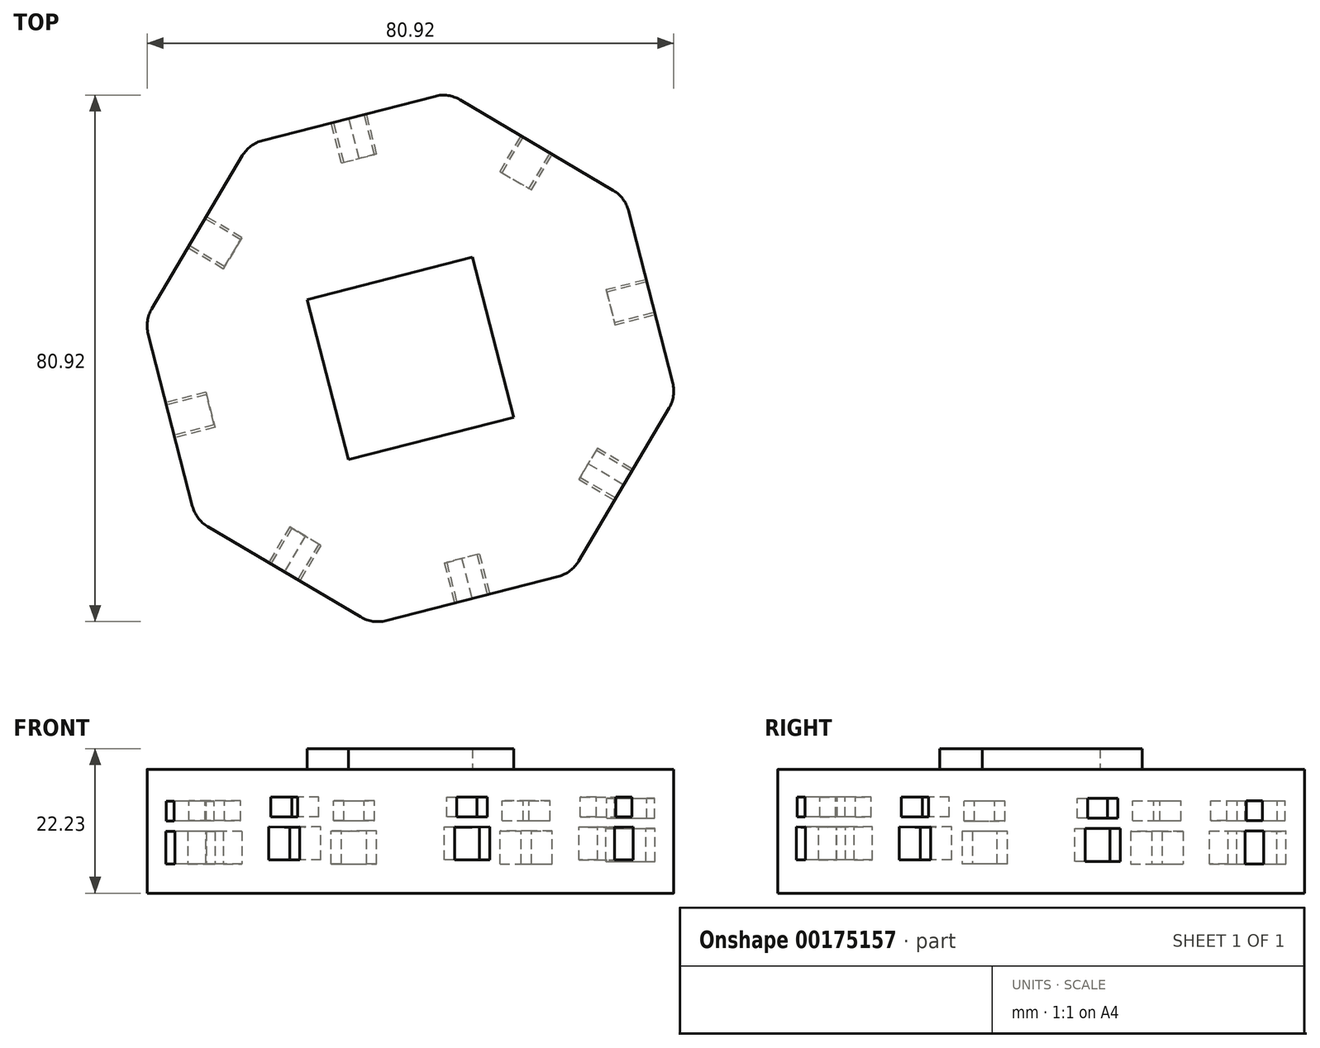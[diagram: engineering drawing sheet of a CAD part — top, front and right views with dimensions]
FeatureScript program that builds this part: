
annotation { "Feature Type Name" : "Feature", "Feature Type Description" : "" }
export const myFeature = defineFeature(function(context is Context, id is Id, definition is map)
    precondition{}
    {
        {
            var Q0;
            Q0=qCreatedBy(makeId("Top.planeOp"),FACE);
            var sketch = newSketch(context, id + "F0", { "sketchPlane" : qUnion([Q0])});
            skCircle(sketch, "E0.cCircle", {"center": v(0, 0) * mm, "radius": 38.1 * mm, "construction": true});
            skLineSegment(sketch, "E0.0", {"start": v(-40.83, 5.82) * mm, "end": v(-24.75, 32.98) * mm});
            skLineSegment(sketch, "E0.1", {"start": v(-24.75, 32.98) * mm, "end": v(5.82, 40.83) * mm});
            skLineSegment(sketch, "E0.2", {"start": v(5.82, 40.83) * mm, "end": v(32.98, 24.75) * mm});
            skLineSegment(sketch, "E0.3", {"start": v(32.98, 24.75) * mm, "end": v(40.83, -5.82) * mm});
            skLineSegment(sketch, "E0.4", {"start": v(40.83, -5.82) * mm, "end": v(24.75, -32.98) * mm});
            skLineSegment(sketch, "E0.5", {"start": v(24.75, -32.98) * mm, "end": v(-5.82, -40.83) * mm});
            skLineSegment(sketch, "E0.6", {"start": v(-5.82, -40.83) * mm, "end": v(-32.98, -24.75) * mm});
            skLineSegment(sketch, "E0.7", {"start": v(-32.98, -24.75) * mm, "end": v(-40.83, 5.82) * mm});
            skPoint(sketch, "E0.0.midPoint", {"position": v(-32.8, 19.4) * mm});
            skLineSegment(sketch, "E1", {"start": v(32.8, -19.4) * mm, "end": v(-32.8, 19.4) * mm});
            skLineSegment(sketch, "E2", {"start": v(9.47, -36.9) * mm, "end": v(-9.47, 36.9) * mm});
            skLineSegment(sketch, "E3", {"start": v(19.4, 32.8) * mm, "end": v(-19.4, -32.8) * mm});
            skLineSegment(sketch, "E4", {"start": v(36.9, 9.47) * mm, "end": v(-36.9, -9.47) * mm});
            skSolve(sketch);
        }
        {
            var Q0;
            Q0=makeQuery(id+"F0.imprint","IMPRINT",FACE,{"disambiguationData":[TD([[makeQuery(id+"F0.imprint","IMPRINT",EDGE,{"derivedFrom":sQuery(id+"F0.wireOp",EDGE,"E0.0")}),-1.0]])]});
            var Q1;
            {var subQ0=sQuery(id+"F0.wireOp",EDGE,"E0.2");var subQ1=sQuery(id+"F0.wireOp",EDGE,"E0.1");var subQ2=makeQuery(id+"F0.imprint","INTERSECT",VERTEX,{"derivedFrom":[subQ1,subQ0]});Q1=makeQuery(id+"F0.imprint","IMPRINT",FACE,{"disambiguationData":[TD([[makeQuery(id+"F0.imprint","IMPRINT",EDGE,{"disambiguationData":[TD([[subQ2,1.0]])],"derivedFrom":subQ1}),-1.0]])]});}
            var Q2;
            {var subQ0=sQuery(id+"F0.wireOp",EDGE,"E0.3");var subQ1=sQuery(id+"F0.wireOp",EDGE,"E0.2");var subQ2=makeQuery(id+"F0.imprint","INTERSECT",VERTEX,{"derivedFrom":[subQ1,subQ0]});Q2=makeQuery(id+"F0.imprint","IMPRINT",FACE,{"disambiguationData":[TD([[makeQuery(id+"F0.imprint","IMPRINT",EDGE,{"disambiguationData":[TD([[subQ2,1.0]])],"derivedFrom":subQ1}),-1.0]])]});}
            var Q3;
            {var subQ0=sQuery(id+"F0.wireOp",EDGE,"E0.4");var subQ1=sQuery(id+"F0.wireOp",EDGE,"E0.3");var subQ2=makeQuery(id+"F0.imprint","INTERSECT",VERTEX,{"derivedFrom":[subQ1,subQ0]});Q3=makeQuery(id+"F0.imprint","IMPRINT",FACE,{"disambiguationData":[TD([[makeQuery(id+"F0.imprint","IMPRINT",EDGE,{"disambiguationData":[TD([[subQ2,1.0]])],"derivedFrom":subQ1}),-1.0]])]});}
            var Q4;
            {var subQ0=sQuery(id+"F0.wireOp",EDGE,"E0.5");var subQ1=sQuery(id+"F0.wireOp",EDGE,"E0.4");var subQ2=makeQuery(id+"F0.imprint","INTERSECT",VERTEX,{"derivedFrom":[subQ1,subQ0]});Q4=makeQuery(id+"F0.imprint","IMPRINT",FACE,{"disambiguationData":[TD([[makeQuery(id+"F0.imprint","IMPRINT",EDGE,{"disambiguationData":[TD([[subQ2,1.0]])],"derivedFrom":subQ1}),-1.0]])]});}
            var Q5;
            {var subQ0=sQuery(id+"F0.wireOp",EDGE,"E0.6");var subQ1=sQuery(id+"F0.wireOp",EDGE,"E0.5");var subQ2=makeQuery(id+"F0.imprint","INTERSECT",VERTEX,{"derivedFrom":[subQ1,subQ0]});Q5=makeQuery(id+"F0.imprint","IMPRINT",FACE,{"disambiguationData":[TD([[makeQuery(id+"F0.imprint","IMPRINT",EDGE,{"disambiguationData":[TD([[subQ2,1.0]])],"derivedFrom":subQ1}),-1.0]])]});}
            var Q6;
            {var subQ0=sQuery(id+"F0.wireOp",EDGE,"E0.7");var subQ1=sQuery(id+"F0.wireOp",EDGE,"E0.6");var subQ2=makeQuery(id+"F0.imprint","INTERSECT",VERTEX,{"derivedFrom":[subQ1,subQ0]});Q6=makeQuery(id+"F0.imprint","IMPRINT",FACE,{"disambiguationData":[TD([[makeQuery(id+"F0.imprint","IMPRINT",EDGE,{"disambiguationData":[TD([[subQ2,1.0]])],"derivedFrom":subQ1}),-1.0]])]});}
            extrude(context, id + "F1", {"entities" : qUnion([Q0, Q1, Q2, Q3, Q4, Q5, Q6]), "endBound" : BoundingType.SYMMETRIC, "depth" : 19.05 * mm});
        }
        {
            var Q0;
            Q0=makeQuery(id+"F1.opExtrude","SWEPT_FACE",FACE,{"disambiguationData":[OSD([sQuery(id+"F0.wireOp",EDGE,"E0.7")])]});
            var sketch = newSketch(context, id + "F2", { "sketchPlane" : qUnion([Q0])});
            skPoint(sketch, "E5.middle", {"position": v(0, 0) * mm});
            skPoint(sketch, "E6", {"position": v(0, -5.06) * mm});
            skLineSegment(sketch, "E7", {"start": v(-2.8, -2.52) * mm, "end": v(-2.8, 0) * mm});
            skLineSegment(sketch, "E8", {"start": v(2.8, -2.52) * mm, "end": v(2.8, 0) * mm});
            skLineSegment(sketch, "E9", {"start": v(-2.8, 0) * mm, "end": v(2.8, 0) * mm});
            skLineSegment(sketch, "E10.MirrorCS", {"start": v(-2.8, -2.52) * mm, "end": v(-2.8, -5.04) * mm});
            skLineSegment(sketch, "E11.MirrorCS", {"start": v(-2.8, -5.04) * mm, "end": v(2.8, -5.04) * mm});
            skLineSegment(sketch, "E12.MirrorCS", {"start": v(2.8, -2.52) * mm, "end": v(2.8, -5.04) * mm});
            skPoint(sketch, "E13", {"position": v(0, 1.56) * mm});
            skLineSegment(sketch, "E14", {"start": v(0, 1.56) * mm, "end": v(-2.41, 1.56) * mm});
            skLineSegment(sketch, "E15.MirrorCS", {"start": v(0, 1.56) * mm, "end": v(2.41, 1.56) * mm});
            skLineSegment(sketch, "E16", {"start": v(2.41, 1.56) * mm, "end": v(2.41, 4.6) * mm});
            skLineSegment(sketch, "E17.MirrorCS", {"start": v(-2.41, 1.56) * mm, "end": v(-2.41, 4.6) * mm});
            skLineSegment(sketch, "E18", {"start": v(-2.41, 4.6) * mm, "end": v(2.41, 4.6) * mm});
            skSolve(sketch);
        }
        {
            var Q0;
            Q0 = qSketchRegion(id + "F2", true);
            extrude(context, id + "F3", {"entities" : qUnion([Q0]), "operationType" : NewBodyOperationType.REMOVE, "oppositeDirection" : true, "depth" : 6.35 * mm});
        }
        {
            var Q0;
            Q0=makeQuery(id+"F1.opExtrude","SWEPT_FACE",FACE,{"disambiguationData":[OSD([sQuery(id+"F0.wireOp",EDGE,"E0.1")])]});
            var sketch = newSketch(context, id + "F4", { "sketchPlane" : qUnion([Q0])});
            skPoint(sketch, "E19", {"position": v(0, -9.53) * mm});
            skPoint(sketch, "E20", {"position": v(0, -5.04) * mm});
            skPoint(sketch, "E21", {"position": v(0, 1.6) * mm});
            skLineSegment(sketch, "E22", {"start": v(0, 1.6) * mm, "end": v(2.41, 1.6) * mm});
            skLineSegment(sketch, "E23", {"start": v(2.41, 1.6) * mm, "end": v(2.41, 4.64) * mm});
            skLineSegment(sketch, "E24", {"start": v(2.41, 4.64) * mm, "end": v(0, 4.64) * mm});
            skLineSegment(sketch, "E25.MirrorCS", {"start": v(-2.41, 4.64) * mm, "end": v(0, 4.64) * mm});
            skLineSegment(sketch, "E26.MirrorCS", {"start": v(-2.41, 1.6) * mm, "end": v(-2.41, 4.64) * mm});
            skLineSegment(sketch, "E27.MirrorCS", {"start": v(0, 1.6) * mm, "end": v(-2.41, 1.6) * mm});
            skLineSegment(sketch, "E28", {"start": v(0, -5.04) * mm, "end": v(2.8, -5.04) * mm});
            skLineSegment(sketch, "E29", {"start": v(2.8, -5.04) * mm, "end": v(2.8, 0.04) * mm});
            skLineSegment(sketch, "E30", {"start": v(2.8, 0.04) * mm, "end": v(0, 0) * mm});
            skLineSegment(sketch, "E31.MirrorCS", {"start": v(-2.8, 0.04) * mm, "end": v(0, 0) * mm});
            skLineSegment(sketch, "E32.MirrorCS", {"start": v(-2.8, -5.04) * mm, "end": v(-2.8, 0.04) * mm});
            skLineSegment(sketch, "E33.MirrorCS", {"start": v(0, -5.04) * mm, "end": v(-2.8, -5.04) * mm});
            skSolve(sketch);
        }
        {
            var Q0;
            Q0=makeQuery(id+"F4.imprint","IMPRINT",FACE,{"disambiguationData":[TD([[makeQuery(id+"F4.imprint","IMPRINT",EDGE,{"derivedFrom":sQuery(id+"F4.wireOp",EDGE,"LZL7hc5V-V0Lx-cx1U-TuNf-BSn2dO84Y1Hg")}),-1.0]])]});
            var Q1;
            Q1=makeQuery(id+"F4.imprint","IMPRINT",FACE,{"disambiguationData":[TD([[makeQuery(id+"F4.imprint","IMPRINT",EDGE,{"derivedFrom":sQuery(id+"F4.wireOp",EDGE,"E28")}),1.0]])]});
            var Q2;
            Q2=makeQuery(id+"F4.imprint","IMPRINT",FACE,{"disambiguationData":[TD([[makeQuery(id+"F4.imprint","IMPRINT",EDGE,{"derivedFrom":sQuery(id+"F4.wireOp",EDGE,"E22")}),1.0]])]});
            extrude(context, id + "F5", {"entities" : qUnion([Q0, Q1, Q2]), "operationType" : NewBodyOperationType.REMOVE, "oppositeDirection" : true, "depth" : 6.35 * mm});
        }
        {
            var Q0;
            Q0=makeQuery(id+"F1.opExtrude","SWEPT_FACE",FACE,{"disambiguationData":[OSD([sQuery(id+"F0.wireOp",EDGE,"E0.0")])]});
            var sketch = newSketch(context, id + "F6", { "sketchPlane" : qUnion([Q0])});
            skPoint(sketch, "E34", {"position": v(0, -5.04) * mm});
            skLineSegment(sketch, "E35", {"start": v(0, -5.04) * mm, "end": v(2.8, -5.04) * mm});
            skLineSegment(sketch, "E36", {"start": v(2.8, 0) * mm, "end": v(2.8, -5.04) * mm});
            skLineSegment(sketch, "E37.MirrorCS", {"start": v(-2.8, 0) * mm, "end": v(-2.8, -5.04) * mm});
            skLineSegment(sketch, "E38.MirrorCS", {"start": v(0, -5.04) * mm, "end": v(-2.8, -5.04) * mm});
            skPoint(sketch, "E39", {"position": v(0, 1.6) * mm});
            skLineSegment(sketch, "E40", {"start": v(-2.8, 0) * mm, "end": v(2.8, 0) * mm});
            skLineSegment(sketch, "E41", {"start": v(0, 1.6) * mm, "end": v(2.41, 1.6) * mm});
            skLineSegment(sketch, "E42", {"start": v(2.41, 1.6) * mm, "end": v(2.41, 4.64) * mm});
            skLineSegment(sketch, "E43", {"start": v(2.41, 4.64) * mm, "end": v(0, 4.64) * mm});
            skLineSegment(sketch, "E44.MirrorCS", {"start": v(-2.41, 4.64) * mm, "end": v(0, 4.64) * mm});
            skLineSegment(sketch, "E45.MirrorCS", {"start": v(-2.41, 1.6) * mm, "end": v(-2.41, 4.64) * mm});
            skLineSegment(sketch, "E46.MirrorCS", {"start": v(0, 1.6) * mm, "end": v(-2.41, 1.6) * mm});
            skSolve(sketch);
        }
        {
            var Q0;
            Q0=makeQuery(id+"F6.imprint","IMPRINT",FACE,{"disambiguationData":[TD([[makeQuery(id+"F6.imprint","IMPRINT",EDGE,{"derivedFrom":sQuery(id+"F6.wireOp",EDGE,"E41")}),1.0]])]});
            var Q1;
            Q1=makeQuery(id+"F6.imprint","IMPRINT",FACE,{"disambiguationData":[TD([[makeQuery(id+"F6.imprint","IMPRINT",EDGE,{"derivedFrom":sQuery(id+"F6.wireOp",EDGE,"E35")}),1.0]])]});
            extrude(context, id + "F7", {"entities" : qUnion([Q0, Q1]), "operationType" : NewBodyOperationType.REMOVE, "oppositeDirection" : true, "depth" : 6.35 * mm});
        }
        {
            var Q0;
            Q0=makeQuery(id+"F1.opExtrude","SWEPT_FACE",FACE,{"disambiguationData":[OSD([sQuery(id+"F0.wireOp",EDGE,"E0.2")])]});
            var sketch = newSketch(context, id + "F8", { "sketchPlane" : qUnion([Q0])});
            skPoint(sketch, "E47", {"position": v(0, -5.04) * mm});
            skLineSegment(sketch, "E48", {"start": v(0, -5.04) * mm, "end": v(2.8, -5.04) * mm});
            skLineSegment(sketch, "E49", {"start": v(2.8, -5.04) * mm, "end": v(2.8, 0.04) * mm});
            skLineSegment(sketch, "E50.MirrorCS", {"start": v(-2.8, -5.04) * mm, "end": v(-2.8, 0.04) * mm});
            skLineSegment(sketch, "E51.MirrorCS", {"start": v(0, -5.04) * mm, "end": v(-2.8, -5.04) * mm});
            skLineSegment(sketch, "E52", {"start": v(-2.8, 0.04) * mm, "end": v(2.8, 0.04) * mm});
            skPoint(sketch, "E53", {"position": v(0, 1.63) * mm});
            skLineSegment(sketch, "E54", {"start": v(0, 1.63) * mm, "end": v(2.41, 1.63) * mm});
            skLineSegment(sketch, "E55", {"start": v(2.41, 1.63) * mm, "end": v(2.41, 4.68) * mm});
            skLineSegment(sketch, "E56.MirrorCS", {"start": v(0, 1.63) * mm, "end": v(-2.41, 1.63) * mm});
            skLineSegment(sketch, "E57.MirrorCS", {"start": v(-2.41, 1.63) * mm, "end": v(-2.41, 4.68) * mm});
            skLineSegment(sketch, "E58", {"start": v(-2.41, 4.68) * mm, "end": v(2.41, 4.68) * mm});
            skSolve(sketch);
        }
        {
            var Q0;
            Q0=makeQuery(id+"F8.imprint","IMPRINT",FACE,{"disambiguationData":[TD([[makeQuery(id+"F8.imprint","IMPRINT",EDGE,{"derivedFrom":sQuery(id+"F8.wireOp",EDGE,"E54")}),1.0]])]});
            var Q1;
            Q1=makeQuery(id+"F8.imprint","IMPRINT",FACE,{"disambiguationData":[TD([[makeQuery(id+"F8.imprint","IMPRINT",EDGE,{"derivedFrom":sQuery(id+"F8.wireOp",EDGE,"E48")}),1.0]])]});
            extrude(context, id + "F9", {"entities" : qUnion([Q0, Q1]), "operationType" : NewBodyOperationType.REMOVE, "oppositeDirection" : true, "depth" : 6.35 * mm});
        }
        {
            var Q0;
            Q0=makeQuery(id+"F1.opExtrude","SWEPT_FACE",FACE,{"disambiguationData":[OSD([sQuery(id+"F0.wireOp",EDGE,"E0.3")])]});
            var sketch = newSketch(context, id + "F10", { "sketchPlane" : qUnion([Q0])});
            skPoint(sketch, "E59", {"position": v(0, -4.7) * mm});
            skLineSegment(sketch, "E60", {"start": v(0, -4.7) * mm, "end": v(2.8, -4.7) * mm});
            skLineSegment(sketch, "E61", {"start": v(2.8, -4.7) * mm, "end": v(2.8, 0.39) * mm});
            skLineSegment(sketch, "E62.MirrorCS", {"start": v(-2.8, -4.7) * mm, "end": v(-2.8, 0.39) * mm});
            skLineSegment(sketch, "E63.MirrorCS", {"start": v(0, -4.7) * mm, "end": v(-2.8, -4.7) * mm});
            skLineSegment(sketch, "E64", {"start": v(-2.8, 0.39) * mm, "end": v(2.8, 0.39) * mm});
            skPoint(sketch, "E65", {"position": v(0, 1.98) * mm});
            skLineSegment(sketch, "E66", {"start": v(0, 1.98) * mm, "end": v(2.41, 1.98) * mm});
            skLineSegment(sketch, "E67", {"start": v(2.41, 1.98) * mm, "end": v(2.41, 5.03) * mm});
            skLineSegment(sketch, "E68.MirrorCS", {"start": v(0, 1.98) * mm, "end": v(-2.41, 1.98) * mm});
            skLineSegment(sketch, "E69.MirrorCS", {"start": v(-2.41, 1.98) * mm, "end": v(-2.41, 5.03) * mm});
            skLineSegment(sketch, "E70", {"start": v(-2.41, 5.03) * mm, "end": v(2.41, 5.03) * mm});
            skSolve(sketch);
        }
        {
            var Q0;
            Q0 = qSketchRegion(id + "F10", true);
            extrude(context, id + "F11", {"entities" : qUnion([Q0]), "operationType" : NewBodyOperationType.REMOVE, "oppositeDirection" : true, "depth" : 6.35 * mm});
        }
        {
            var Q0;
            Q0=makeQuery(id+"F1.opExtrude","SWEPT_FACE",FACE,{"disambiguationData":[OSD([sQuery(id+"F0.wireOp",EDGE,"E0.4")])]});
            var sketch = newSketch(context, id + "F12", { "sketchPlane" : qUnion([Q0])});
            skPoint(sketch, "E71", {"position": v(0, -8.9) * mm});
            skPoint(sketch, "E72", {"position": v(0, -4.42) * mm});
            skPoint(sketch, "E73", {"position": v(0, 2.22) * mm});
            skLineSegment(sketch, "E74", {"start": v(0, 2.22) * mm, "end": v(2.41, 2.22) * mm});
            skLineSegment(sketch, "E75", {"start": v(2.41, 2.22) * mm, "end": v(2.41, 5.26) * mm});
            skLineSegment(sketch, "E76", {"start": v(2.41, 5.26) * mm, "end": v(0, 5.26) * mm});
            skLineSegment(sketch, "E77.MirrorCS", {"start": v(-2.41, 5.26) * mm, "end": v(0, 5.26) * mm});
            skLineSegment(sketch, "E78.MirrorCS", {"start": v(-2.41, 2.22) * mm, "end": v(-2.41, 5.26) * mm});
            skLineSegment(sketch, "E79.MirrorCS", {"start": v(0, 2.22) * mm, "end": v(-2.41, 2.22) * mm});
            skLineSegment(sketch, "E80", {"start": v(0, -4.42) * mm, "end": v(2.8, -4.42) * mm});
            skLineSegment(sketch, "E81", {"start": v(2.8, -4.42) * mm, "end": v(2.8, 0.66) * mm});
            skLineSegment(sketch, "E82", {"start": v(2.8, 0.66) * mm, "end": v(0, 0.62) * mm});
            skLineSegment(sketch, "E83.MirrorCS", {"start": v(-2.8, 0.66) * mm, "end": v(0, 0.62) * mm});
            skLineSegment(sketch, "E84.MirrorCS", {"start": v(-2.8, -4.42) * mm, "end": v(-2.8, 0.66) * mm});
            skLineSegment(sketch, "E85.MirrorCS", {"start": v(0, -4.42) * mm, "end": v(-2.8, -4.42) * mm});
            skSolve(sketch);
        }
        {
            var Q0;
            Q0=makeQuery(id+"F12.imprint","IMPRINT",FACE,{"disambiguationData":[TD([[makeQuery(id+"F12.imprint","IMPRINT",EDGE,{"derivedFrom":sQuery(id+"F12.wireOp",EDGE,"E80")}),1.0]])]});
            var Q1;
            Q1=makeQuery(id+"F12.imprint","IMPRINT",FACE,{"disambiguationData":[TD([[makeQuery(id+"F12.imprint","IMPRINT",EDGE,{"derivedFrom":sQuery(id+"F12.wireOp",EDGE,"E74")}),1.0]])]});
            extrude(context, id + "F13", {"entities" : qUnion([Q0, Q1]), "operationType" : NewBodyOperationType.REMOVE, "oppositeDirection" : true, "depth" : 6.35 * mm});
        }
        {
            var Q0;
            Q0=makeQuery(id+"F1.opExtrude","SWEPT_FACE",FACE,{"disambiguationData":[OSD([sQuery(id+"F0.wireOp",EDGE,"E0.5")])]});
            var sketch = newSketch(context, id + "F14", { "sketchPlane" : qUnion([Q0])});
            skPoint(sketch, "E86", {"position": v(0, -8.9) * mm});
            skPoint(sketch, "E87", {"position": v(0, -4.42) * mm});
            skPoint(sketch, "E88", {"position": v(0, 2.22) * mm});
            skLineSegment(sketch, "E89", {"start": v(0, 2.22) * mm, "end": v(2.41, 2.22) * mm});
            skLineSegment(sketch, "E90", {"start": v(2.41, 2.22) * mm, "end": v(2.41, 5.26) * mm});
            skLineSegment(sketch, "E91", {"start": v(2.41, 5.26) * mm, "end": v(0, 5.26) * mm});
            skLineSegment(sketch, "E92.MirrorCS", {"start": v(-2.41, 5.26) * mm, "end": v(0, 5.26) * mm});
            skLineSegment(sketch, "E93.MirrorCS", {"start": v(-2.41, 2.22) * mm, "end": v(-2.41, 5.26) * mm});
            skLineSegment(sketch, "E94.MirrorCS", {"start": v(0, 2.22) * mm, "end": v(-2.41, 2.22) * mm});
            skLineSegment(sketch, "E95", {"start": v(0, -4.42) * mm, "end": v(2.8, -4.42) * mm});
            skLineSegment(sketch, "E96", {"start": v(2.8, -4.42) * mm, "end": v(2.8, 0.66) * mm});
            skLineSegment(sketch, "E97", {"start": v(2.8, 0.66) * mm, "end": v(0, 0.62) * mm});
            skLineSegment(sketch, "E98.MirrorCS", {"start": v(-2.8, 0.66) * mm, "end": v(0, 0.62) * mm});
            skLineSegment(sketch, "E99.MirrorCS", {"start": v(-2.8, -4.42) * mm, "end": v(-2.8, 0.66) * mm});
            skLineSegment(sketch, "E100.MirrorCS", {"start": v(0, -4.42) * mm, "end": v(-2.8, -4.42) * mm});
            skSolve(sketch);
        }
        {
            var Q0;
            Q0=makeQuery(id+"F14.imprint","IMPRINT",FACE,{"disambiguationData":[TD([[makeQuery(id+"F14.imprint","IMPRINT",EDGE,{"derivedFrom":sQuery(id+"F14.wireOp",EDGE,"E95")}),1.0]])]});
            var Q1;
            Q1=makeQuery(id+"F14.imprint","IMPRINT",FACE,{"disambiguationData":[TD([[makeQuery(id+"F14.imprint","IMPRINT",EDGE,{"derivedFrom":sQuery(id+"F14.wireOp",EDGE,"E89")}),1.0]])]});
            extrude(context, id + "F15", {"entities" : qUnion([Q0, Q1]), "operationType" : NewBodyOperationType.REMOVE, "oppositeDirection" : true, "depth" : 6.35 * mm});
        }
        {
            var Q0;
            Q0=makeQuery(id+"F1.opExtrude","SWEPT_FACE",FACE,{"disambiguationData":[OSD([sQuery(id+"F0.wireOp",EDGE,"E0.6")])]});
            var sketch = newSketch(context, id + "F16", { "sketchPlane" : qUnion([Q0])});
            skPoint(sketch, "E101", {"position": v(0, -8.9) * mm});
            skPoint(sketch, "E102", {"position": v(0, -4.42) * mm});
            skPoint(sketch, "E103", {"position": v(0, 2.22) * mm});
            skLineSegment(sketch, "E104", {"start": v(0, 2.22) * mm, "end": v(2.41, 2.22) * mm});
            skLineSegment(sketch, "E105", {"start": v(2.41, 2.22) * mm, "end": v(2.41, 5.26) * mm});
            skLineSegment(sketch, "E106", {"start": v(2.41, 5.26) * mm, "end": v(0, 5.26) * mm});
            skLineSegment(sketch, "E107.MirrorCS", {"start": v(-2.41, 5.26) * mm, "end": v(0, 5.26) * mm});
            skLineSegment(sketch, "E108.MirrorCS", {"start": v(-2.41, 2.22) * mm, "end": v(-2.41, 5.26) * mm});
            skLineSegment(sketch, "E109.MirrorCS", {"start": v(0, 2.22) * mm, "end": v(-2.41, 2.22) * mm});
            skLineSegment(sketch, "E110", {"start": v(0, -4.42) * mm, "end": v(2.8, -4.42) * mm});
            skLineSegment(sketch, "E111", {"start": v(2.8, -4.42) * mm, "end": v(2.8, 0.66) * mm});
            skLineSegment(sketch, "E112", {"start": v(2.8, 0.66) * mm, "end": v(0, 0.62) * mm});
            skLineSegment(sketch, "E113.MirrorCS", {"start": v(-2.8, 0.66) * mm, "end": v(0, 0.62) * mm});
            skLineSegment(sketch, "E114.MirrorCS", {"start": v(-2.8, -4.42) * mm, "end": v(-2.8, 0.66) * mm});
            skLineSegment(sketch, "E115.MirrorCS", {"start": v(0, -4.42) * mm, "end": v(-2.8, -4.42) * mm});
            skSolve(sketch);
        }
        {
            var Q0;
            Q0=makeQuery(id+"F16.imprint","IMPRINT",FACE,{"disambiguationData":[TD([[makeQuery(id+"F16.imprint","IMPRINT",EDGE,{"derivedFrom":sQuery(id+"F16.wireOp",EDGE,"E104")}),1.0]])]});
            var Q1;
            Q1=makeQuery(id+"F16.imprint","IMPRINT",FACE,{"disambiguationData":[TD([[makeQuery(id+"F16.imprint","IMPRINT",EDGE,{"derivedFrom":sQuery(id+"F16.wireOp",EDGE,"E110")}),1.0]])]});
            extrude(context, id + "F17", {"entities" : qUnion([Q0, Q1]), "operationType" : NewBodyOperationType.REMOVE, "oppositeDirection" : true, "depth" : 6.35 * mm});
        }
        {
            var Q0;
            Q0=makeQuery(id+"F1.opExtrude","CAP_FACE",FACE,{"disambiguationData":[OSD([sQuery(id+"F0.wireOp",EDGE,"E0.0"),sQuery(id+"F0.wireOp",EDGE,"E0.1"),sQuery(id+"F0.wireOp",EDGE,"E0.2"),sQuery(id+"F0.wireOp",EDGE,"E0.3"),sQuery(id+"F0.wireOp",EDGE,"E0.4"),sQuery(id+"F0.wireOp",EDGE,"E0.5"),sQuery(id+"F0.wireOp",EDGE,"E0.6"),sQuery(id+"F0.wireOp",EDGE,"E0.7")])],"isStart":false});
            var sketch = newSketch(context, id + "F18", { "sketchPlane" : qUnion([Q0])});
            skLineSegment(sketch, "E116", {"start": v(-24.75, 32.98) * mm, "end": v(-5.82, -40.83) * mm});
            skLineSegment(sketch, "E117", {"start": v(5.82, 40.83) * mm, "end": v(24.75, -32.98) * mm});
            skLineSegment(sketch, "E118", {"start": v(3.16, -12.3) * mm, "end": v(-12.13, -16.22) * mm});
            skLineSegment(sketch, "E119", {"start": v(3.16, -12.3) * mm, "end": v(18.44, -8.38) * mm});
            skLineSegment(sketch, "E120", {"start": v(-3.16, 12.3) * mm, "end": v(-18.44, 8.38) * mm});
            skLineSegment(sketch, "E121", {"start": v(-3.16, 12.3) * mm, "end": v(12.13, 16.22) * mm});
            skPoint(sketch, "E122", {"position": v(-15.86, 9.04) * mm});
            skPoint(sketch, "E123", {"position": v(9.54, 15.56) * mm});
            skPoint(sketch, "E124", {"position": v(-9.54, -15.56) * mm});
            skPoint(sketch, "E125", {"position": v(15.86, -9.04) * mm});
            skLineSegment(sketch, "E126", {"start": v(-15.86, 9.04) * mm, "end": v(-9.54, -15.56) * mm});
            skLineSegment(sketch, "E127", {"start": v(9.54, 15.56) * mm, "end": v(15.86, -9.04) * mm});
            skSolve(sketch);
        }
        {
            var Q0;
            {var subQ4=sQuery(id+"F18.wireOp",EDGE,"E126");Q0=makeQuery(id+"F18.imprint","IMPRINT",FACE,{"disambiguationData":[TD([[makeQuery(id+"F18.imprint","IMPRINT",EDGE,{"derivedFrom":subQ4}),1.0]])]});}
            extrude(context, id + "F19", {"entities" : qUnion([Q0]), "operationType" : NewBodyOperationType.ADD, "depth" : 3.17 * mm});
        }
        {
            var Q0;
            Q0=makeQuery(id+"F1.opExtrude","SWEPT_EDGE",EDGE,{"disambiguationData":[OSD([sQuery(id+"F0.wireOp",EDGE,"E0.5"),sQuery(id+"F0.wireOp",EDGE,"E0.6")])]});
            var Q1;
            Q1=makeQuery(id+"F1.opExtrude","SWEPT_EDGE",EDGE,{"disambiguationData":[OSD([sQuery(id+"F0.wireOp",EDGE,"E0.4"),sQuery(id+"F0.wireOp",EDGE,"E0.5")])]});
            var Q2;
            Q2=makeQuery(id+"F1.opExtrude","SWEPT_EDGE",EDGE,{"disambiguationData":[OSD([sQuery(id+"F0.wireOp",EDGE,"E0.3"),sQuery(id+"F0.wireOp",EDGE,"E0.4")])]});
            var Q3;
            Q3=makeQuery(id+"F1.opExtrude","SWEPT_EDGE",EDGE,{"disambiguationData":[OSD([sQuery(id+"F0.wireOp",EDGE,"E0.2"),sQuery(id+"F0.wireOp",EDGE,"E0.3")])]});
            var Q4;
            Q4=makeQuery(id+"F1.opExtrude","SWEPT_EDGE",EDGE,{"disambiguationData":[OSD([sQuery(id+"F0.wireOp",EDGE,"E0.1"),sQuery(id+"F0.wireOp",EDGE,"E0.2")])]});
            var Q5;
            Q5=makeQuery(id+"F1.opExtrude","SWEPT_EDGE",EDGE,{"disambiguationData":[OSD([sQuery(id+"F0.wireOp",EDGE,"E0.0"),sQuery(id+"F0.wireOp",EDGE,"E0.1")])]});
            var Q6;
            Q6=makeQuery(id+"F1.opExtrude","SWEPT_EDGE",EDGE,{"disambiguationData":[OSD([sQuery(id+"F0.wireOp",EDGE,"E0.0"),sQuery(id+"F0.wireOp",EDGE,"E0.7")])]});
            var Q7;
            Q7=makeQuery(id+"F1.opExtrude","SWEPT_EDGE",EDGE,{"disambiguationData":[OSD([sQuery(id+"F0.wireOp",EDGE,"E0.6"),sQuery(id+"F0.wireOp",EDGE,"E0.7")])]});
            fillet(context, id + "F20", {"entities" : qUnion([Q0, Q1, Q2, Q3, Q4, Q5, Q6, Q7]), "radius" : 5.08 * mm, "tangentPropagation" : true, "allowEdgeOverflow" : false});
        }
    });
